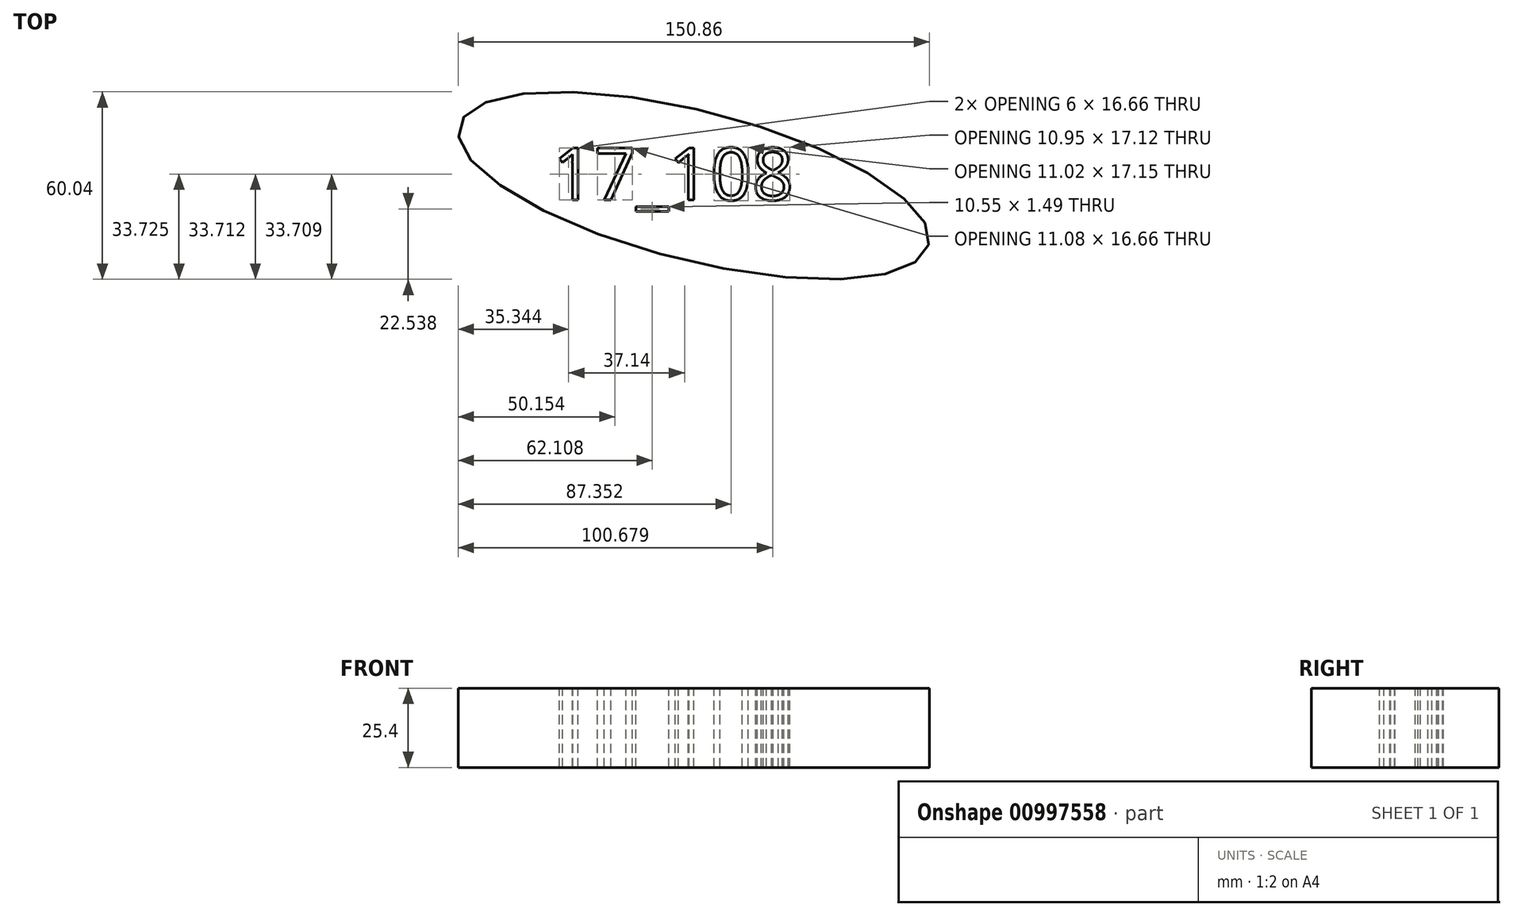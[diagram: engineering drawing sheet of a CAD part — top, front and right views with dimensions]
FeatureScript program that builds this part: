
annotation { "Feature Type Name" : "Feature", "Feature Type Description" : "" }
export const myFeature = defineFeature(function(context is Context, id is Id, definition is map)
    precondition{}
    {
        {
            var Q0;
            Q0=qCreatedBy(makeId("Top.planeOp"),FACE);
            var sketch = newSketch(context, id + "F0", { "sketchPlane" : qUnion([Q0])});
            skEllipse(sketch, "E0", {"center": v(0, 0) * mm, "majorRadius": 77.56 * mm, "minorRadius": 23.97 * mm, "majorAxis": v(0.97, -0.24)});
            skSolve(sketch);
        }
        {
            var Q0;
            Q0 = qSketchRegion(id + "F0", true);
            extrude(context, id + "F1", {"entities" : qUnion([Q0]), "depth" : 25.4 * mm, "offsetDistance" : 25.4 * mm});
        }
        {
            var Q0;
            Q0=makeQuery(id+"F1.opExtrude","CAP_FACE",FACE,{"disambiguationData":[OSD([sQuery(id+"F0.wireOp",EDGE,"E0")])],"isStart":false});
            var sketch = newSketch(context, id + "F2", { "sketchPlane" : qUnion([Q0])});
            skText(sketch, "E1", { "text": "17_108", "fontName": "OpenSans-Regular.ttf"});
            const initialGuessF2  = {"E1": [-0.04523, -0.00464, 1, 0, 0.0168]};
            skSetInitialGuess(sketch, initialGuessF2);
            skSolve(sketch);
        }
        {
            var Q0;
            Q0 = qSketchRegion(id + "F2", true);
            extrude(context, id + "F3", {"entities" : qUnion([Q0]), "operationType" : NewBodyOperationType.REMOVE, "oppositeDirection" : true, "depth" : 25.4 * mm, "offsetDistance" : 25.4 * mm});
        }
    });
